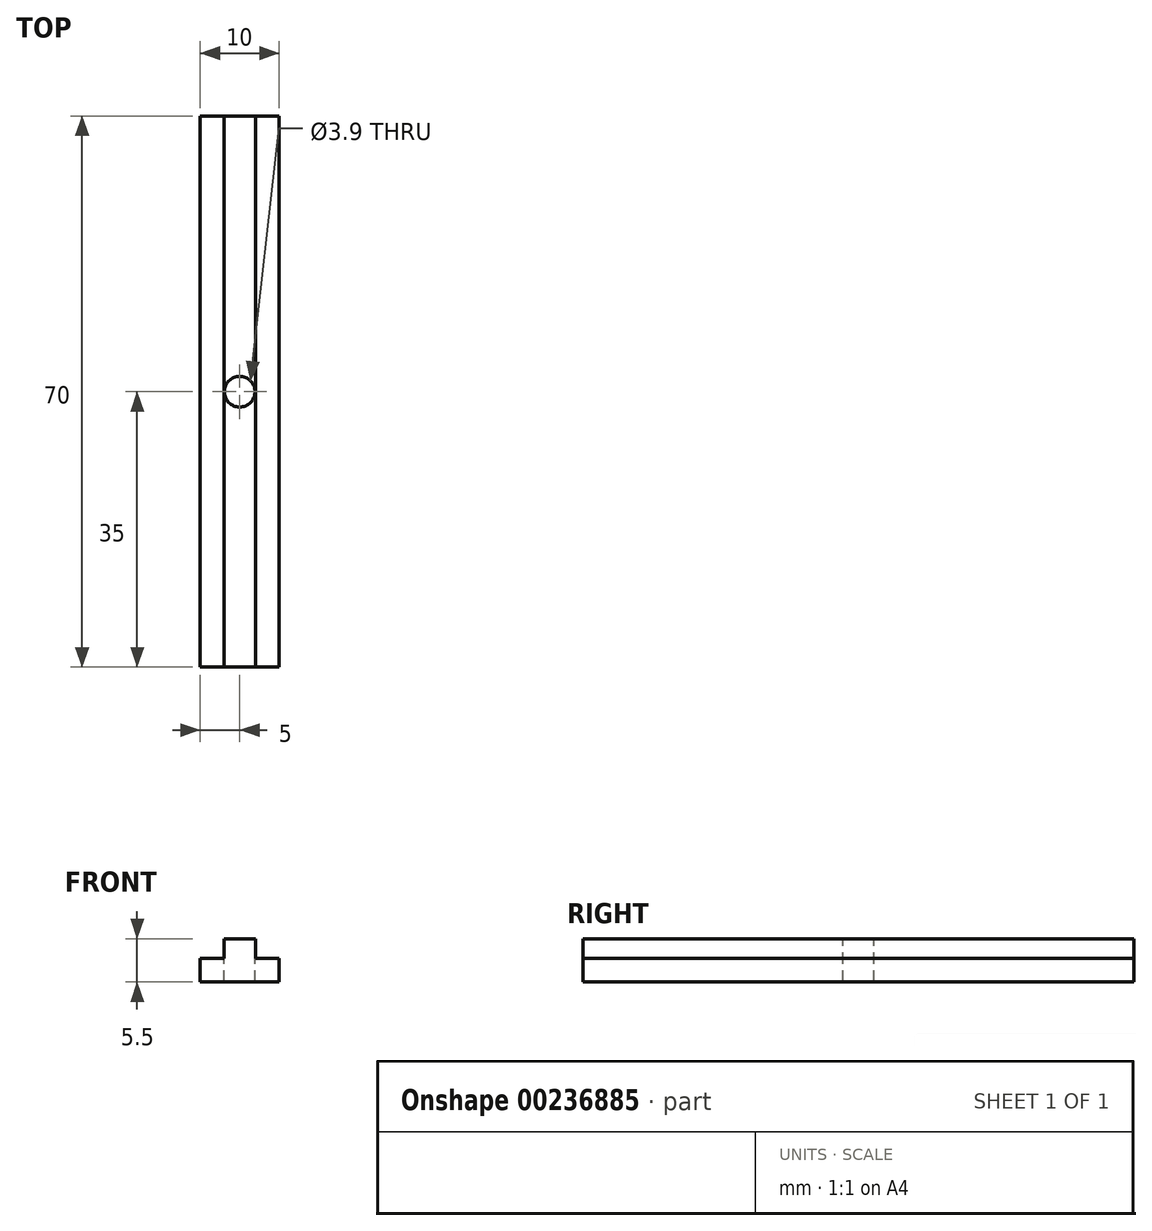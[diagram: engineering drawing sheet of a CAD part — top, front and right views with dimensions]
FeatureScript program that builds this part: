
annotation { "Feature Type Name" : "Feature", "Feature Type Description" : "" }
export const myFeature = defineFeature(function(context is Context, id is Id, definition is map)
    precondition{}
    {
        {
            var Q0;
            Q0=qCreatedBy(makeId("Front.planeOp"),FACE);
            var sketch = newSketch(context, id + "F0", { "sketchPlane" : qUnion([Q0])});
            skLineSegment(sketch, "E0.bottom", {"start": v(-5, -2.75) * mm, "end": v(5, -2.75) * mm});
            skLineSegment(sketch, "E0.left", {"start": v(-5, -2.75) * mm, "end": v(-5, 0.25) * mm});
            skLineSegment(sketch, "E0.right", {"start": v(5, -2.75) * mm, "end": v(5, 0.25) * mm});
            skLineSegment(sketch, "E1", {"start": v(2.12, 0.25) * mm, "end": v(5, 0.25) * mm});
            skLineSegment(sketch, "E2", {"start": v(-2, 0.25) * mm, "end": v(-5, 0.25) * mm});
            skLineSegment(sketch, "E3", {"start": v(-2, 2.75) * mm, "end": v(-2, 0.25) * mm});
            skLineSegment(sketch, "E4", {"start": v(-2, 2.75) * mm, "end": v(0, 2.75) * mm});
            skLineSegment(sketch, "E5.MirrorCS", {"start": v(2, 2.75) * mm, "end": v(0, 2.75) * mm});
            skLineSegment(sketch, "E6.MirrorCS", {"start": v(2, 2.75) * mm, "end": v(2, 0.25) * mm});
            skLineSegment(sketch, "E7", {"start": v(2, 0.25) * mm, "end": v(2.12, 0.25) * mm});
            skSolve(sketch);
        }
        {
            var Q0;
            Q0 = qSketchRegion(id + "F0", true);
            extrude(context, id + "F1", {"entities" : qUnion([Q0]), "depth" : 70 * mm});
        }
        {
            var Q0;
            Q0=makeQuery(id+"F1.opExtrude","SWEPT_FACE",FACE,{"disambiguationData":[OSD([sQuery(id+"F0.wireOp",EDGE,"E4"),sQuery(id+"F0.wireOp",EDGE,"E5.MirrorCS")])]});
            var sketch = newSketch(context, id + "F2", { "sketchPlane" : qUnion([Q0])});
            skCircle(sketch, "E8", {"center": v(0, -35) * mm, "radius": 1.95 * mm});
            skSolve(sketch);
        }
        {
            var Q0;
            Q0 = qSketchRegion(id + "F2", true);
            extrude(context, id + "F3", {"entities" : qUnion([Q0]), "operationType" : NewBodyOperationType.REMOVE, "oppositeDirection" : true, "depth" : 25 * mm});
        }
    });
